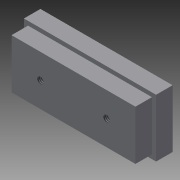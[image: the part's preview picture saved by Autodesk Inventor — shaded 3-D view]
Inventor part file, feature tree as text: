
AUTODESK INVENTOR PART (.ipt)
format: ipt  version: 2014 (Build 180170000, 170)  size: 93,696 bytes
history: native  units: in
note: dims shown in document units (in); Inventor stores cm internally (conversion verified against a paired STEP export)
features: sketch x3, extrude x2, hole x1
ambient origin geometry x8: Origin, YZ Plane, XZ Plane, XY Plane, X Axis, Y Axis, Z Axis, Center Point
bodies: Solid1 (feature_tree)
feature tree (6):
  extrude  "Extrusion1"  Depth=1.75in
  extrude  "Extrusion2"  Depth=0.125in
  hole  "Hole1"  [1 undecoded]
  sketch  "Sketch1"  dims[d0=4.0in d1=1.75in]
  sketch  "Sketch2"  dims[d2=1.0in d3=0.0in d4=0.125in]
  sketch  "Sketch3"  dims[d5=0.5in d6=0.0in d7=2.0in d8=1.0in d9=1.0in d10=0.875in d11=0.196in d12=1.0in d13=0.375in d14=0.25in d15=0.5635in d16=1.0in d17=0.8108in]
note: 1 required parameter value undecoded (feature->parameter linkage not recoverable at this tier; creation-order binding heuristic only, values carry confidence <= 0.55)
